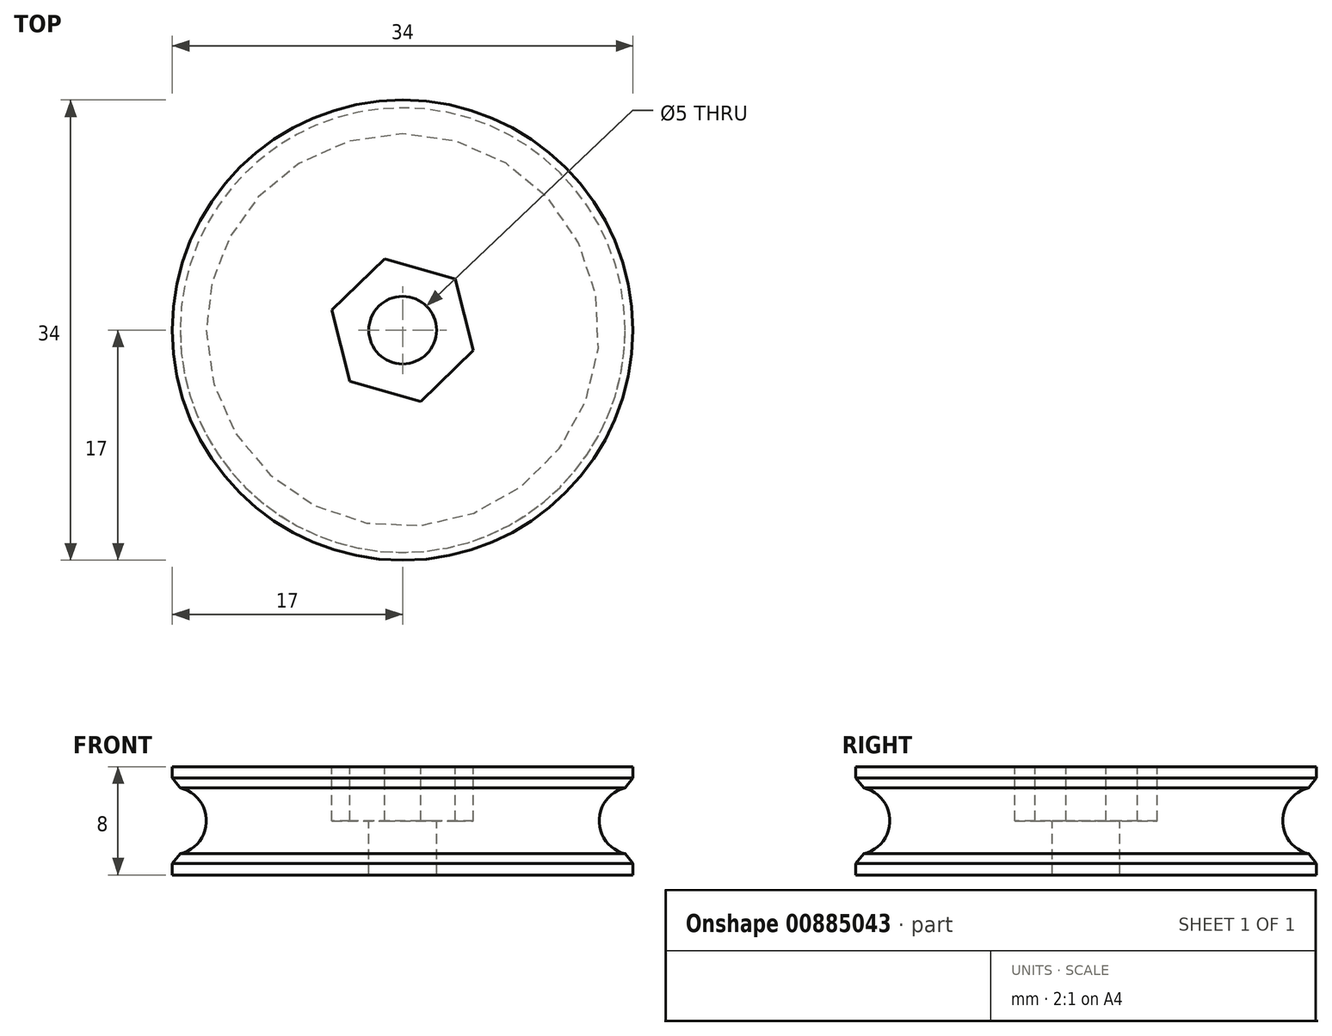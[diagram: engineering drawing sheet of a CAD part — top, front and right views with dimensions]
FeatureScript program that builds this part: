
annotation { "Feature Type Name" : "Feature", "Feature Type Description" : "" }
export const myFeature = defineFeature(function(context is Context, id is Id, definition is map)
    precondition{}
    {
        {
            var Q0;
            Q0=qCreatedBy(makeId("Top.planeOp"),FACE);
            var sketch = newSketch(context, id + "F0", { "sketchPlane" : qUnion([Q0])});
            skCircle(sketch, "E0", {"center": v(0, 0) * mm, "radius": 17 * mm});
            skSolve(sketch);
        }
        {
            var Q0;
            Q0 = qSketchRegion(id + "F0", true);
            extrude(context, id + "F1", {"entities" : qUnion([Q0]), "endBound" : BoundingType.SYMMETRIC, "depth" : 8 * mm, "offsetDistance" : 25 * mm});
        }
        {
            var Q0;
            Q0=makeQuery(id+"F1.opExtrude","CAP_FACE",FACE,{"disambiguationData":[OSD([sQuery(id+"F0.wireOp",EDGE,"E0")])],"isStart":false});
            var sketch = newSketch(context, id + "F2", { "sketchPlane" : qUnion([Q0])});
            skCircle(sketch, "E1", {"center": v(0, 0) * mm, "radius": 2.5 * mm});
            skSolve(sketch);
        }
        {
            var Q0;
            Q0 = qSketchRegion(id + "F2", true);
            extrude(context, id + "F3", {"entities" : qUnion([Q0]), "operationType" : NewBodyOperationType.REMOVE, "oppositeDirection" : true, "depth" : 25 * mm, "offsetDistance" : 25 * mm});
        }
        {
            var Q0;
            Q0=makeQuery(id+"F1.opExtrude","CAP_FACE",FACE,{"disambiguationData":[OSD([sQuery(id+"F0.wireOp",EDGE,"E0")])],"isStart":false});
            var sketch = newSketch(context, id + "F4", { "sketchPlane" : qUnion([Q0])});
            skCircle(sketch, "E2.cCircle", {"center": v(0, 0) * mm, "radius": 4.7 * mm, "construction": true});
            skLineSegment(sketch, "E2.0", {"start": v(3.9, 3.78) * mm, "end": v(5.22, -1.48) * mm});
            skLineSegment(sketch, "E2.1", {"start": v(5.22, -1.48) * mm, "end": v(1.33, -5.26) * mm});
            skLineSegment(sketch, "E2.2", {"start": v(1.33, -5.26) * mm, "end": v(-3.9, -3.78) * mm});
            skLineSegment(sketch, "E2.3", {"start": v(-3.9, -3.78) * mm, "end": v(-5.22, 1.48) * mm});
            skLineSegment(sketch, "E2.4", {"start": v(-5.22, 1.48) * mm, "end": v(-1.33, 5.26) * mm});
            skLineSegment(sketch, "E2.5", {"start": v(-1.33, 5.26) * mm, "end": v(3.9, 3.78) * mm});
            skPoint(sketch, "E2.0.midPoint", {"position": v(4.56, 1.15) * mm});
            skSolve(sketch);
        }
        {
            var Q0;
            Q0 = qSketchRegion(id + "F4", true);
            extrude(context, id + "F5", {"entities" : qUnion([Q0]), "operationType" : NewBodyOperationType.REMOVE, "oppositeDirection" : true, "depth" : 4 * mm, "offsetDistance" : 25 * mm});
        }
        {
            var Q0;
            Q0=qCreatedBy(makeId("Right.planeOp"),FACE);
            var sketch = newSketch(context, id + "F6", { "sketchPlane" : qUnion([Q0])});
            skLineSegment(sketch, "E3", {"start": v(-22.1, 0) * mm, "end": v(24.04, 0) * mm, "construction": true});
            skLineSegment(sketch, "E4", {"start": v(-17, -4) * mm, "end": v(-17, 4) * mm, "construction": true});
            skLineSegment(sketch, "E5", {"start": v(17, 4) * mm, "end": v(17, -4) * mm, "construction": true});
            skCircle(sketch, "E6", {"center": v(-17, 0) * mm, "radius": 2.5 * mm});
            skSolve(sketch);
        }
        {
            var Q0;
            Q0 = qSketchRegion(id + "F6", true);
            var Q1;
            Q1=makeQuery(id+"F5.boolean.opBoolean","INTERSECT",EDGE,{"derivedFrom":[makeQuery(id+"F3.boolean.opBoolean","COPY",FACE,{"derivedFrom":makeQuery(id+"F3.opExtrude","SWEPT_FACE",FACE,{"disambiguationData":[OSD([sQuery(id+"F2.wireOp",EDGE,"E1")])]})}),makeQuery(id+"F5.opExtrude","CAP_FACE",FACE,{"disambiguationData":[OSD([sQuery(id+"F4.wireOp",EDGE,"E2.0"),sQuery(id+"F4.wireOp",EDGE,"E2.1"),sQuery(id+"F4.wireOp",EDGE,"E2.2"),sQuery(id+"F4.wireOp",EDGE,"E2.3"),sQuery(id+"F4.wireOp",EDGE,"E2.4"),sQuery(id+"F4.wireOp",EDGE,"E2.5")])],"isStart":false})]});
            revolve(context, id + "F7", {"operationType" : NewBodyOperationType.REMOVE, "surfaceOperationType" : NewSurfaceOperationType.NEW, "entities" : qUnion([Q0]), "axis" : qUnion([Q1]), "revolveType" : RevolveType.FULL});
        }
        {
            var Q0;
            Q0=makeQuery(id+"F7.boolean.opBoolean","INTERSECT",EDGE,{"disambiguationData":[OD(1.0)],"derivedFrom":[makeQuery(id+"F1.opExtrude","SWEPT_FACE",FACE,{"disambiguationData":[OSD([sQuery(id+"F0.wireOp",EDGE,"E0")])]}),makeQuery(id+"F7.opRevolve","SWEPT_FACE",FACE,{"disambiguationData":[OSD([sQuery(id+"F6.wireOp",EDGE,"E6")])]})]});
            var Q1;
            Q1=makeQuery(id+"F7.boolean.opBoolean","INTERSECT",EDGE,{"disambiguationData":[OD(0.0)],"derivedFrom":[makeQuery(id+"F1.opExtrude","SWEPT_FACE",FACE,{"disambiguationData":[OSD([sQuery(id+"F0.wireOp",EDGE,"E0")])]}),makeQuery(id+"F7.opRevolve","SWEPT_FACE",FACE,{"disambiguationData":[OSD([sQuery(id+"F6.wireOp",EDGE,"E6")])]})]});
            chamfer(context, id + "F8", {"entities" : qUnion([Q0, Q1]), "width" : .75 * mm, "tangentPropagation" : true});
        }
    });
